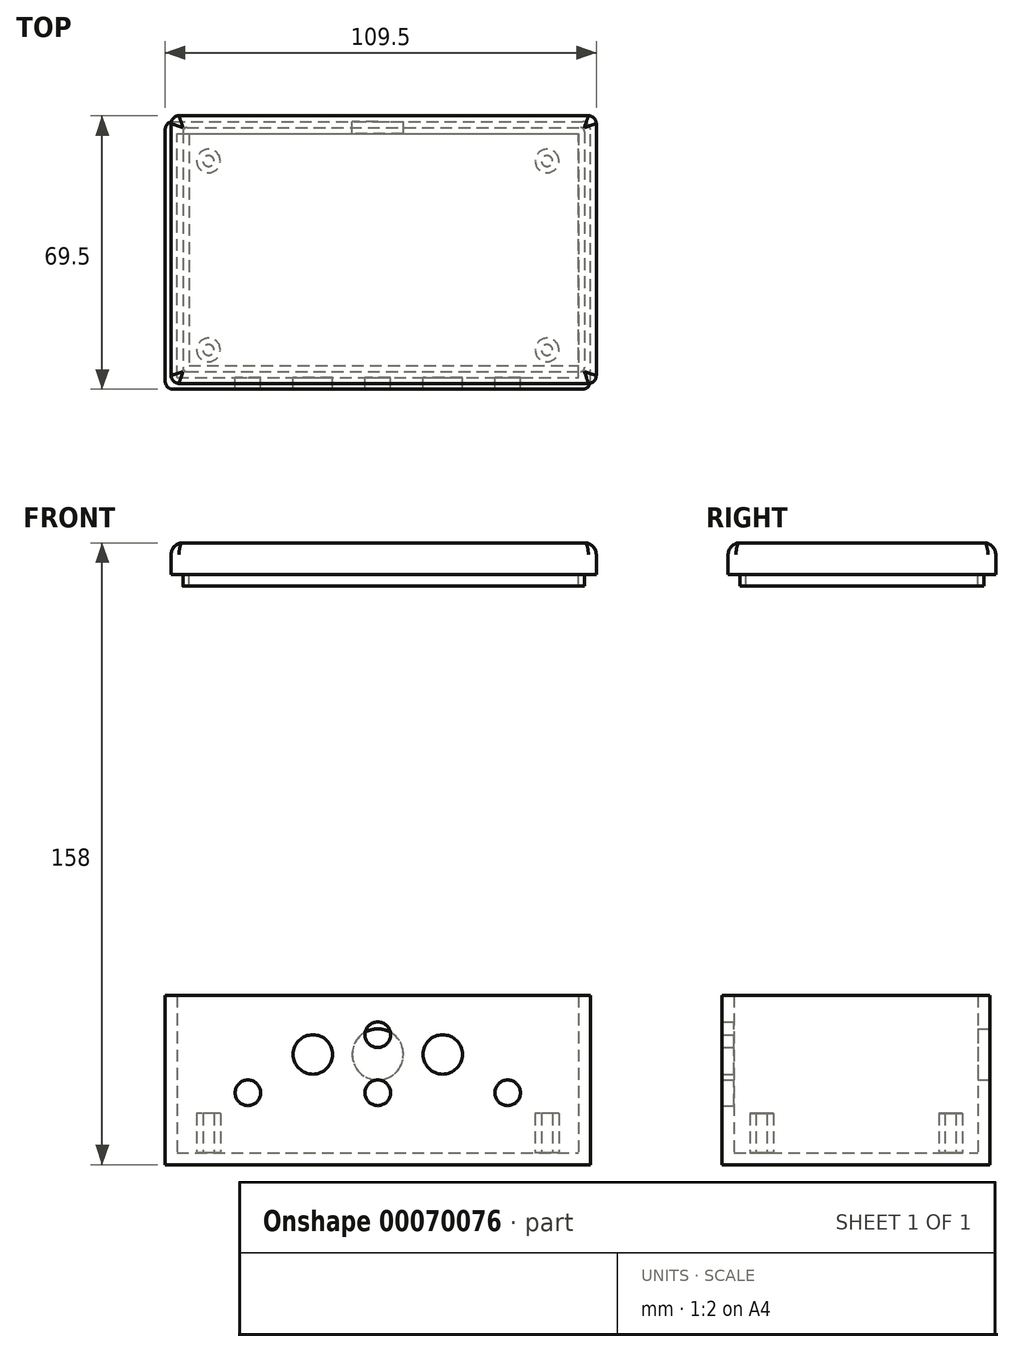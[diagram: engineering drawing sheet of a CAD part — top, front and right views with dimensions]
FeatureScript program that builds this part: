
annotation { "Feature Type Name" : "Feature", "Feature Type Description" : "" }
export const myFeature = defineFeature(function(context is Context, id is Id, definition is map)
    precondition{}
    {
        {
            var Q0;
            Q0=qCreatedBy(makeId("Top.planeOp"),FACE);
            cPlane(context, id + "F0", {"entities" : qUnion([Q0]), "cplaneType" : CPlaneType.OFFSET, "offset" : 150 * mm, "width" : 150 * mm, "height" : 150 * mm});
        }
        {
            var Q0;
            Q0=qCreatedBy(makeId("Front.planeOp"),FACE);
            cPlane(context, id + "F1", {"entities" : qUnion([Q0]), "cplaneType" : CPlaneType.OFFSET, "offset" : 65 * mm, "oppositeDirection" : true, "width" : 150 * mm, "height" : 150 * mm});
        }
        {
            var Q0;
            Q0=qCreatedBy(makeId("Top.planeOp"),FACE);
            var sketch = newSketch(context, id + "F2", { "sketchPlane" : qUnion([Q0])});
            skLineSegment(sketch, "E0.bottom", {"start": v(0, 0) * mm, "end": v(102, 0) * mm});
            skLineSegment(sketch, "E0.top", {"start": v(0, 62) * mm, "end": v(102, 62) * mm});
            skLineSegment(sketch, "E0.left", {"start": v(0, 0) * mm, "end": v(0, 62) * mm});
            skLineSegment(sketch, "E0.right", {"start": v(102, 0) * mm, "end": v(102, 62) * mm});
            skSolve(sketch);
        }
        {
            var Q0;
            Q0=qCreatedBy(makeId("Top.planeOp"),FACE);
            var sketch = newSketch(context, id + "F3", { "sketchPlane" : qUnion([Q0])});
            skLineSegment(sketch, "E1.bottom", {"start": v(-1, -3) * mm, "end": v(103, -3) * mm});
            skLineSegment(sketch, "E1.top", {"start": v(-1, 65) * mm, "end": v(103, 65) * mm});
            skLineSegment(sketch, "E1.left", {"start": v(-3, -1) * mm, "end": v(-3, 63) * mm});
            skLineSegment(sketch, "E1.right", {"start": v(105, -1) * mm, "end": v(105, 63) * mm});
            skPoint(sketch, "E2.visualSharp", {"position": v(-3, 65) * mm});
            skArc(sketch, "E2.filletArc", {"start": v(-1, 65) * mm, "mid": v(-2.41, 64.41) * mm, "end": v(-3, 63) * mm});
            skPoint(sketch, "E3.visualSharp", {"position": v(105, 65) * mm});
            skArc(sketch, "E3.filletArc", {"start": v(105, 63) * mm, "mid": v(104.41, 64.41) * mm, "end": v(103, 65) * mm});
            skPoint(sketch, "E4.visualSharp", {"position": v(105, -3) * mm});
            skArc(sketch, "E4.filletArc", {"start": v(103, -3) * mm, "mid": v(104.41, -2.41) * mm, "end": v(105, -1) * mm});
            skPoint(sketch, "E5.visualSharp", {"position": v(-3, -3) * mm});
            skArc(sketch, "E5.filletArc", {"start": v(-3, -1) * mm, "mid": v(-2.41, -2.41) * mm, "end": v(-1, -3) * mm});
            skSolve(sketch);
        }
        {
            var Q0;
            Q0 = qSketchRegion(id + "F3", true);
            extrude(context, id + "F4", {"entities" : qUnion([Q0]), "oppositeDirection" : true, "depth" : 3 * mm});
        }
        {
            var Q0;
            Q0=makeQuery(id+"F3.imprint","IMPRINT",FACE,{"disambiguationData":[TD([[makeQuery(id+"F3.imprint","IMPRINT",EDGE,{"derivedFrom":sQuery(id+"F3.wireOp",EDGE,"E1.bottom")}),1.0]])]});
            extrude(context, id + "F5", {"entities" : qUnion([Q0]), "operationType" : NewBodyOperationType.ADD, "depth" : 40 * mm});
        }
        {
            var Q0;
            Q0 = qSketchRegion(id + "F2", true);
            extrude(context, id + "F6", {"entities" : qUnion([Q0]), "operationType" : NewBodyOperationType.REMOVE, "depth" : 40 * mm});
        }
        {
            var Q0;
            Q0=qCreatedBy(makeId("Top.planeOp"),FACE);
            var sketch = newSketch(context, id + "F7", { "sketchPlane" : qUnion([Q0])});
            skLineSegment(sketch, "E6.bottom", {"start": v(0, 0) * mm, "end": v(102, 0) * mm});
            skLineSegment(sketch, "E6.top", {"start": v(0, 62) * mm, "end": v(102, 62) * mm});
            skLineSegment(sketch, "E6.left", {"start": v(0, 0) * mm, "end": v(0, 62) * mm});
            skLineSegment(sketch, "E6.right", {"start": v(102, 0) * mm, "end": v(102, 62) * mm});
            skCircle(sketch, "E7", {"center": v(8, 7) * mm, "radius": 3 * mm});
            skCircle(sketch, "E8", {"center": v(8, 55) * mm, "radius": 3 * mm});
            skCircle(sketch, "E9", {"center": v(94, 55) * mm, "radius": 3 * mm});
            skCircle(sketch, "E10", {"center": v(94, 7) * mm, "radius": 3 * mm});
            skSolve(sketch);
        }
        {
            var Q0;
            Q0=makeQuery(id+"F7.imprint","IMPRINT",FACE,{"disambiguationData":[TD([[makeQuery(id+"F7.imprint","IMPRINT",EDGE,{"derivedFrom":sQuery(id+"F7.wireOp",EDGE,"E8")}),1.0]])]});
            var Q1;
            Q1=makeQuery(id+"F7.imprint","IMPRINT",FACE,{"disambiguationData":[TD([[makeQuery(id+"F7.imprint","IMPRINT",EDGE,{"derivedFrom":sQuery(id+"F7.wireOp",EDGE,"E7")}),1.0]])]});
            var Q2;
            Q2=makeQuery(id+"F7.imprint","IMPRINT",FACE,{"disambiguationData":[TD([[makeQuery(id+"F7.imprint","IMPRINT",EDGE,{"derivedFrom":sQuery(id+"F7.wireOp",EDGE,"E9")}),1.0]])]});
            var Q3;
            Q3=makeQuery(id+"F7.imprint","IMPRINT",FACE,{"disambiguationData":[TD([[makeQuery(id+"F7.imprint","IMPRINT",EDGE,{"derivedFrom":sQuery(id+"F7.wireOp",EDGE,"E10")}),1.0]])]});
            extrude(context, id + "F8", {"entities" : qUnion([Q0, Q1, Q2, Q3]), "operationType" : NewBodyOperationType.ADD, "depth" : 10 * mm});
        }
        {
            var Q0;
            Q0=qCreatedBy(makeId("Top.planeOp"),FACE);
            var sketch = newSketch(context, id + "F9", { "sketchPlane" : qUnion([Q0])});
            skCircle(sketch, "E11", {"center": v(8, 55) * mm, "radius": 1.4 * mm});
            skCircle(sketch, "E12", {"center": v(94, 55) * mm, "radius": 1.4 * mm});
            skCircle(sketch, "E13", {"center": v(94, 7) * mm, "radius": 1.4 * mm});
            skCircle(sketch, "E14", {"center": v(8, 7) * mm, "radius": 1.4 * mm});
            skSolve(sketch);
        }
        {
            var Q0;
            Q0 = qSketchRegion(id + "F9", true);
            extrude(context, id + "F10", {"entities" : qUnion([Q0]), "operationType" : NewBodyOperationType.REMOVE, "depth" : 40 * mm});
        }
        {
            var Q0;
            Q0=qCreatedBy(makeId("Front.planeOp"),FACE);
            var sketch = newSketch(context, id + "F11", { "sketchPlane" : qUnion([Q0])});
            skCircle(sketch, "E15", {"center": v(18, 15.25) * mm, "radius": 3.25 * mm});
            skCircle(sketch, "E16", {"center": v(51, 15.25) * mm, "radius": 3.25 * mm});
            skCircle(sketch, "E17", {"center": v(84, 15.25) * mm, "radius": 3.25 * mm});
            skCircle(sketch, "E18", {"center": v(51, 30) * mm, "radius": 3.25 * mm});
            skCircle(sketch, "E19", {"center": v(34.5, 25) * mm, "radius": 5 * mm});
            skCircle(sketch, "E20", {"center": v(67.5, 25) * mm, "radius": 5 * mm});
            skSolve(sketch);
        }
        {
            var Q0;
            Q0 = qSketchRegion(id + "F11", true);
            extrude(context, id + "F12", {"entities" : qUnion([Q0]), "operationType" : NewBodyOperationType.REMOVE, "depth" : 10 * mm});
        }
        {
            var Q0;
            Q0=qCreatedBy(id+"F1.planeOp",FACE);
            var sketch = newSketch(context, id + "F13", { "sketchPlane" : qUnion([Q0])});
            skCircle(sketch, "E21", {"center": v(51, 25) * mm, "radius": 6.5 * mm});
            skSolve(sketch);
        }
        {
            var Q0;
            Q0 = qSketchRegion(id + "F13", true);
            extrude(context, id + "F14", {"entities" : qUnion([Q0]), "operationType" : NewBodyOperationType.REMOVE, "depth" : 5 * mm});
        }
        {
            var Q0;
            Q0=qCreatedBy(id+"F0.planeOp",FACE);
            var sketch = newSketch(context, id + "F15", { "sketchPlane" : qUnion([Q0])});
            skLineSegment(sketch, "E22.bottom", {"start": v(0.5, -1.5) * mm, "end": v(104.5, -1.5) * mm});
            skLineSegment(sketch, "E22.top", {"start": v(0.5, 66.5) * mm, "end": v(104.5, 66.5) * mm});
            skLineSegment(sketch, "E22.left", {"start": v(-1.5, 0.5) * mm, "end": v(-1.5, 64.5) * mm});
            skLineSegment(sketch, "E22.right", {"start": v(106.5, 0.5) * mm, "end": v(106.5, 64.5) * mm});
            skPoint(sketch, "E23.visualSharp", {"position": v(-1.5, 66.5) * mm});
            skArc(sketch, "E23.filletArc", {"start": v(0.5, 66.5) * mm, "mid": v(-0.91, 65.91) * mm, "end": v(-1.5, 64.5) * mm});
            skPoint(sketch, "E24.visualSharp", {"position": v(106.5, 66.5) * mm});
            skArc(sketch, "E24.filletArc", {"start": v(106.5, 64.5) * mm, "mid": v(105.91, 65.91) * mm, "end": v(104.5, 66.5) * mm});
            skPoint(sketch, "E25.visualSharp", {"position": v(106.5, -1.5) * mm});
            skArc(sketch, "E25.filletArc", {"start": v(104.5, -1.5) * mm, "mid": v(105.91, -0.91) * mm, "end": v(106.5, 0.5) * mm});
            skPoint(sketch, "E26.visualSharp", {"position": v(-1.5, -1.5) * mm});
            skArc(sketch, "E26.filletArc", {"start": v(-1.5, 0.5) * mm, "mid": v(-0.91, -0.91) * mm, "end": v(0.5, -1.5) * mm});
            skSolve(sketch);
        }
        {
            var Q0;
            Q0=makeQuery(id+"F15.imprint","IMPRINT",FACE,{"disambiguationData":[TD([[makeQuery(id+"F15.imprint","IMPRINT",EDGE,{"derivedFrom":sQuery(id+"F15.wireOp",EDGE,"E22.bottom")}),1.0]])]});
            extrude(context, id + "F16", {"entities" : qUnion([Q0]), "depth" : 5 * mm, "hasSecondDirection" : true, "secondDirectionOppositeDirection" : true, "secondDirectionDepth" : 3 * mm});
        }
        {
            var Q0;
            Q0=makeQuery(id+"F16.opExtrude","CAP_FACE",FACE,{"disambiguationData":[OSD([sQuery(id+"F15.wireOp",EDGE,"E22.bottom"),sQuery(id+"F15.wireOp",EDGE,"E22.top"),sQuery(id+"F15.wireOp",EDGE,"E22.left"),sQuery(id+"F15.wireOp",EDGE,"E22.right"),sQuery(id+"F15.wireOp",EDGE,"E23.filletArc"),sQuery(id+"F15.wireOp",EDGE,"E24.filletArc"),sQuery(id+"F15.wireOp",EDGE,"E25.filletArc"),sQuery(id+"F15.wireOp",EDGE,"E26.filletArc")])],"isStart":true});
            var sketch = newSketch(context, id + "F17", { "sketchPlane" : qUnion([Q0])});
            skLineSegment(sketch, "E27.bottom", {"start": v(2.5, -63.5) * mm, "end": v(102.5, -63.5) * mm});
            skLineSegment(sketch, "E27.top", {"start": v(2.5, -1.5) * mm, "end": v(102.5, -1.5) * mm});
            skLineSegment(sketch, "E27.left", {"start": v(1.5, -62.5) * mm, "end": v(1.5, -2.5) * mm});
            skLineSegment(sketch, "E27.right", {"start": v(103.5, -62.5) * mm, "end": v(103.5, -2.5) * mm});
            skLineSegment(sketch, "E28.bottom", {"start": v(3, -62) * mm, "end": v(102, -62) * mm});
            skLineSegment(sketch, "E28.top", {"start": v(3, -3) * mm, "end": v(102, -3) * mm});
            skLineSegment(sketch, "E28.left", {"start": v(3, -62) * mm, "end": v(3, -3) * mm});
            skLineSegment(sketch, "E28.right", {"start": v(102, -62) * mm, "end": v(102, -3) * mm});
            skPoint(sketch, "E29.visualSharp", {"position": v(103.5, -1.5) * mm});
            skArc(sketch, "E29.filletArc", {"start": v(103.5, -2.5) * mm, "mid": v(103.2, -1.8) * mm, "end": v(102.5, -1.5) * mm});
            skPoint(sketch, "E30.visualSharp", {"position": v(103.5, -63.5) * mm});
            skArc(sketch, "E30.filletArc", {"start": v(102.5, -63.5) * mm, "mid": v(103.2, -63.2) * mm, "end": v(103.5, -62.5) * mm});
            skPoint(sketch, "E31.visualSharp", {"position": v(1.5, -63.5) * mm});
            skArc(sketch, "E31.filletArc", {"start": v(1.5, -62.5) * mm, "mid": v(1.8, -63.2) * mm, "end": v(2.5, -63.5) * mm});
            skArc(sketch, "E32.filletArc", {"start": v(2.5, -1.5) * mm, "mid": v(1.8, -1.8) * mm, "end": v(1.5, -2.5) * mm});
            skSolve(sketch);
        }
        {
            var Q0;
            Q0 = qSketchRegion(id + "F17", true);
            extrude(context, id + "F18", {"entities" : qUnion([Q0]), "operationType" : NewBodyOperationType.ADD, "depth" : 3 * mm});
        }
        {
            var Q0;
            Q0=makeQuery(id+"F16.opExtrude","CAP_EDGE",EDGE,{"disambiguationData":[OSD([sQuery(id+"F15.wireOp",EDGE,"E22.left")])],"isStart":false});
            fillet(context, id + "F19", {"entities" : qUnion([Q0]), "radius" : 3 * mm, "tangentPropagation" : true, "allowEdgeOverflow" : false});
        }
    });
